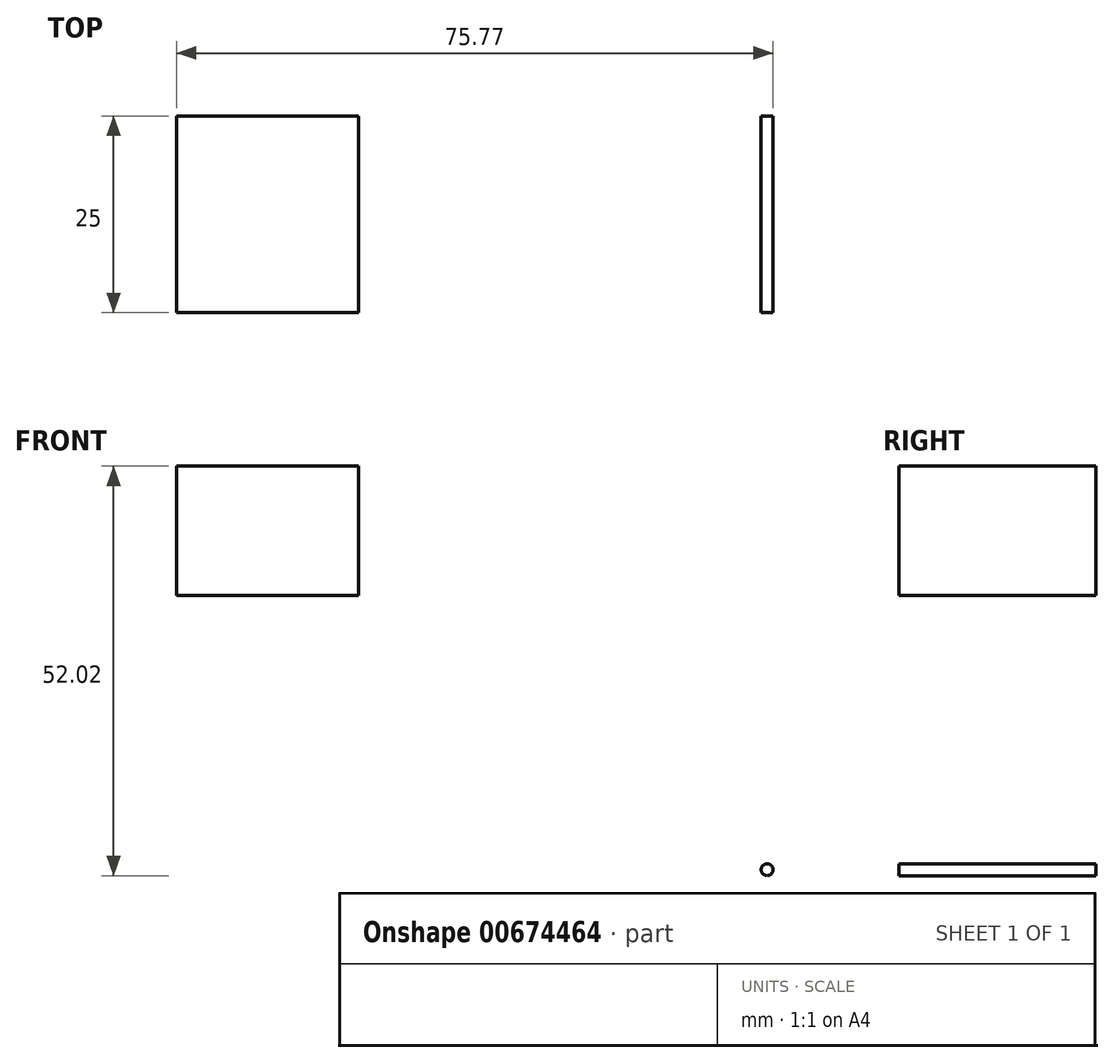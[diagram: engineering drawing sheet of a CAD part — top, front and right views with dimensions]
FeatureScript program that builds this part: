
annotation { "Feature Type Name" : "Feature", "Feature Type Description" : "" }
export const myFeature = defineFeature(function(context is Context, id is Id, definition is map)
    precondition{}
    {
        {
            var Q0;
            Q0=qCreatedBy(makeId("Front.planeOp"),FACE);
            var sketch = newSketch(context, id + "F0", { "sketchPlane" : qUnion([Q0])});
            skLineSegment(sketch, "E0", {"start": v(-18.18, 0) * mm, "end": v(31.82, 0) * mm});
            skLineSegment(sketch, "E1", {"start": v(31.82, 0) * mm, "end": v(31.82, 3) * mm});
            skCircle(sketch, "E2", {"center": v(32.57, 3) * mm, "radius": 0.75 * mm});
            skLineSegment(sketch, "E3.bottom", {"start": v(-42.45, 54.27) * mm, "end": v(-19.3, 54.27) * mm});
            skLineSegment(sketch, "E3.top", {"start": v(-42.45, 37.87) * mm, "end": v(-19.3, 37.87) * mm});
            skLineSegment(sketch, "E3.left", {"start": v(-42.45, 54.27) * mm, "end": v(-42.45, 37.87) * mm});
            skLineSegment(sketch, "E3.right", {"start": v(-19.3, 54.27) * mm, "end": v(-19.3, 37.87) * mm});
            skSolve(sketch);
        }
        {
            var Q0;
            Q0 = qSketchRegion(id + "F0", true);
            extrude(context, id + "F1", {"entities" : qUnion([Q0]), "depth" : 25 * mm, "offsetDistance" : 25 * mm});
        }
    });
